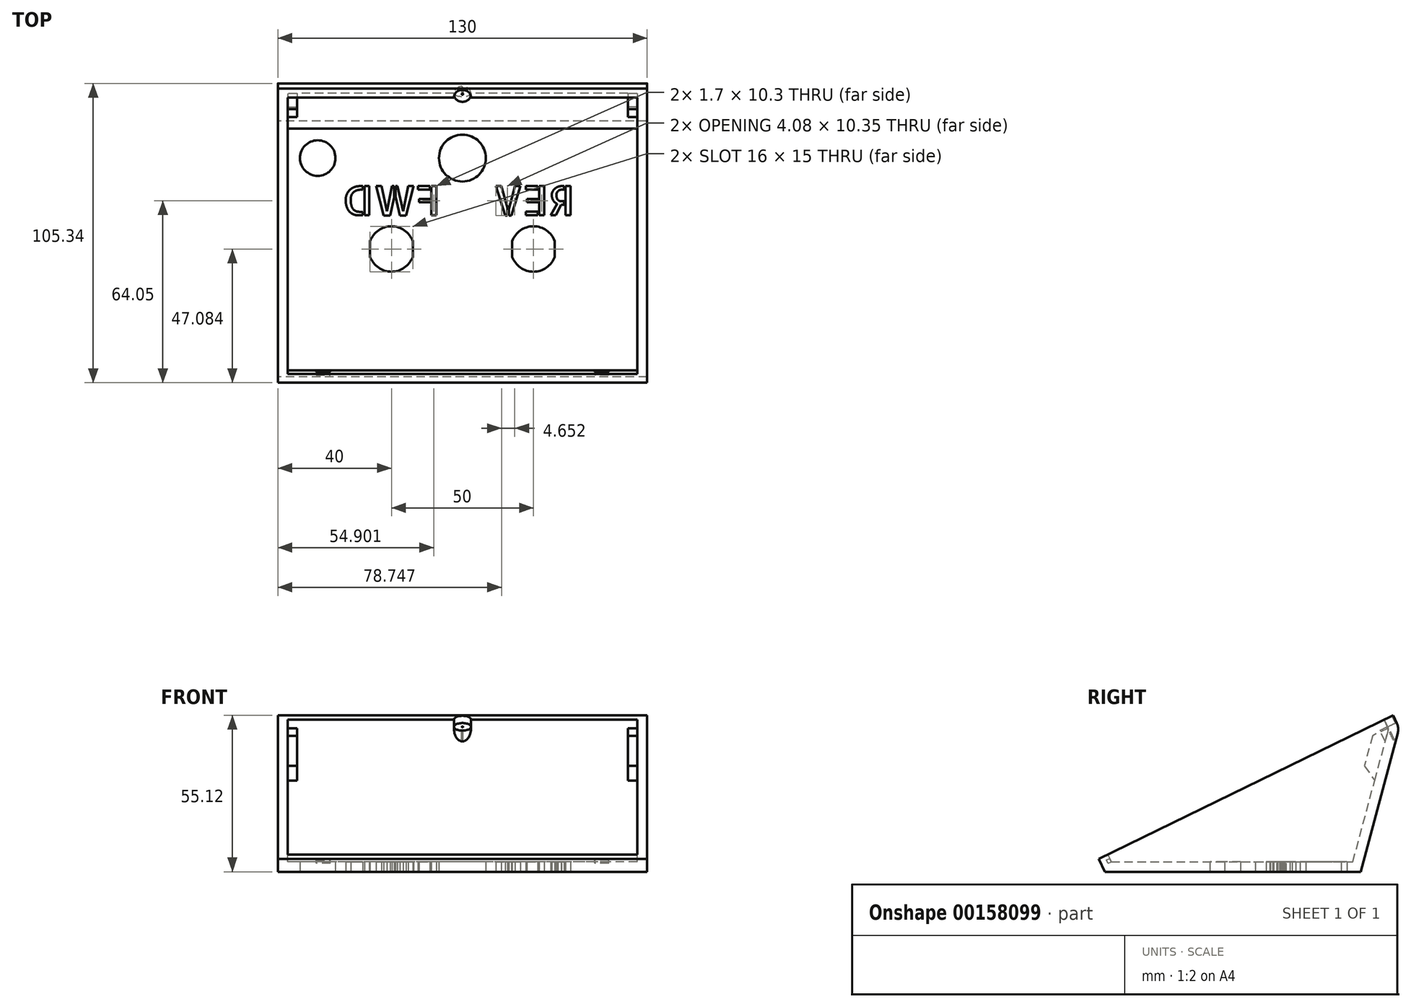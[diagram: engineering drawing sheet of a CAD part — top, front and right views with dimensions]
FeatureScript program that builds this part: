
annotation { "Feature Type Name" : "Feature", "Feature Type Description" : "" }
export const myFeature = defineFeature(function(context is Context, id is Id, definition is map)
    precondition{}
    {
        {
            var Q0;
            Q0=qCreatedBy(makeId("Right.planeOp"),FACE);
            var sketch = newSketch(context, id + "F0", { "sketchPlane" : qUnion([Q0])});
            skLineSegment(sketch, "E0", {"start": v(-41.87, 0) * mm, "end": v(48.13, 0) * mm});
            skLineSegment(sketch, "E1", {"start": v(48.13, 0) * mm, "end": v(61.22, 48.83) * mm});
            skLineSegment(sketch, "E2", {"start": v(60.93, 52.22) * mm, "end": v(59.6, 55.12) * mm});
            skLineSegment(sketch, "E3", {"start": v(59.6, 55.12) * mm, "end": v(-43.95, 4.54) * mm});
            skLineSegment(sketch, "E4", {"start": v(-43.95, 4.54) * mm, "end": v(-41.87, 0) * mm});
            skPoint(sketch, "E5.visualSharp", {"position": v(61.69, 50.58) * mm});
            skArc(sketch, "E5.filletArc", {"start": v(61.22, 48.83) * mm, "mid": v(61.37, 50.55) * mm, "end": v(60.93, 52.22) * mm});
            skSolve(sketch);
        }
        {
            var Q0;
            Q0=makeQuery(id+"F0.imprint","IMPRINT",FACE,{"disambiguationData":[TD([[makeQuery(id+"F0.imprint","IMPRINT",EDGE,{"derivedFrom":sQuery(id+"F0.wireOp",EDGE,"E0")}),1.0]])]});
            extrude(context, id + "F1", {"entities" : qUnion([Q0]), "depth" : 130 * mm});
        }
        {
            var Q0;
            Q0=makeQuery(id+"F1.opExtrude","SWEPT_FACE",FACE,{"disambiguationData":[OSD([sQuery(id+"F0.wireOp",EDGE,"E3")])]});
            shell(context, id + "F2", {"entities" : qUnion([Q0]), "thickness" : 3.5 * mm});
        }
        {
            var Q0;
            Q0=qCreatedBy(makeId("Top.planeOp"),FACE);
            var sketch = newSketch(context, id + "F3", { "sketchPlane" : qUnion([Q0])});
            skCircle(sketch, "E6", {"center": v(90, 3.13) * mm, "radius": 8 * mm});
            skPoint(sketch, "E7", {"position": v(82.5, 5.92) * mm});
            skPoint(sketch, "E8", {"position": v(82.5, 0.35) * mm});
            skPoint(sketch, "E9", {"position": v(97.5, 5.92) * mm});
            skPoint(sketch, "E10", {"position": v(97.5, 0.35) * mm});
            skLineSegment(sketch, "E11", {"start": v(82.5, 5.92) * mm, "end": v(82.5, 0.35) * mm});
            skLineSegment(sketch, "E12", {"start": v(97.5, 5.92) * mm, "end": v(97.5, 0.35) * mm});
            skCircle(sketch, "E13", {"center": v(40, 3.13) * mm, "radius": 8 * mm});
            skPoint(sketch, "E14", {"position": v(32.5, 5.92) * mm});
            skPoint(sketch, "E15", {"position": v(32.5, 0.35) * mm});
            skPoint(sketch, "E16", {"position": v(47.5, 5.92) * mm});
            skPoint(sketch, "E17", {"position": v(47.5, 0.35) * mm});
            skLineSegment(sketch, "E18", {"start": v(32.5, 5.92) * mm, "end": v(32.5, 0.35) * mm});
            skLineSegment(sketch, "E19", {"start": v(47.5, 5.92) * mm, "end": v(47.5, 0.35) * mm});
            skPoint(sketch, "E20", {"position": v(65, 3.3) * mm});
            skCircle(sketch, "E21", {"center": v(65, 35.13) * mm, "radius": 8.25 * mm});
            skCircle(sketch, "E22", {"center": v(14.06, 35.13) * mm, "radius": 6.25 * mm});
            skSolve(sketch);
        }
        {
            var Q0;
            {var subQ0=sQuery(id+"F3.wireOp",EDGE,"E11");Q0=makeQuery(id+"F3.imprint","IMPRINT",FACE,{"disambiguationData":[TD([[makeQuery(id+"F3.imprint","IMPRINT",EDGE,{"derivedFrom":subQ0}),1.0]])]});}
            var Q1;
            {var subQ0=sQuery(id+"F3.wireOp",EDGE,"E18");Q1=makeQuery(id+"F3.imprint","IMPRINT",FACE,{"disambiguationData":[TD([[makeQuery(id+"F3.imprint","IMPRINT",EDGE,{"derivedFrom":subQ0}),1.0]])]});}
            extrude(context, id + "F4", {"entities" : qUnion([Q0, Q1]), "operationType" : NewBodyOperationType.REMOVE, "depth" : 3.5 * mm});
        }
        {
            var Q0;
            Q0=qCreatedBy(makeId("Top.planeOp"),FACE);
            var sketch = newSketch(context, id + "F5", { "sketchPlane" : qUnion([Q0])});
            skText(sketch, "E23", { "text": "FWD", "fontName": "AllertaStencil-Regular.ttf"});
            skText(sketch, "E24", { "text": "REV", "fontName": "AllertaStencil-Regular.ttf"});
            skPoint(sketch, "E25", {"position": v(65, 28.3) * mm});
            const initialGuessF5  = {"E23": [0.07292, 0.01798, 1, 0, 0.0103], "E24": [0.02573, 0.01798, 1, 0, 0.0103]};
            skSetInitialGuess(sketch, initialGuessF5);
            skSolve(sketch);
        }
        {
            var Q0;
            Q0 = qSketchRegion(id + "F5", true);
            extrude(context, id + "F6", {"entities" : qUnion([Q0]), "depth" : 5 * mm});
        }
        {
            var Q0;
            Q0=makeQuery(id+"F6.opExtrude","SWEPT_BODY",BODY,{"disambiguationData":[OSD([sQuery(id+"F5.wireOp",EDGE,"E23.sketch_text.stroke-0"),sQuery(id+"F5.wireOp",EDGE,"E23.sketch_text.stroke-1"),sQuery(id+"F5.wireOp",EDGE,"E23.sketch_text.stroke-2"),sQuery(id+"F5.wireOp",EDGE,"E23.sketch_text.stroke-3")])]});
            var Q1;
            Q1=makeQuery(id+"F6.opExtrude","SWEPT_BODY",BODY,{"disambiguationData":[OSD([sQuery(id+"F5.wireOp",EDGE,"E23.sketch_text.stroke-4"),sQuery(id+"F5.wireOp",EDGE,"E23.sketch_text.stroke-5"),sQuery(id+"F5.wireOp",EDGE,"E23.sketch_text.stroke-6"),sQuery(id+"F5.wireOp",EDGE,"E23.sketch_text.stroke-7")])]});
            var Q2;
            Q2=makeQuery(id+"F6.opExtrude","SWEPT_BODY",BODY,{"disambiguationData":[OSD([sQuery(id+"F5.wireOp",EDGE,"E23.sketch_text.stroke-8"),sQuery(id+"F5.wireOp",EDGE,"E23.sketch_text.stroke-9"),sQuery(id+"F5.wireOp",EDGE,"E23.sketch_text.stroke-10"),sQuery(id+"F5.wireOp",EDGE,"E23.sketch_text.stroke-11")])]});
            var Q3;
            Q3=makeQuery(id+"F6.opExtrude","SWEPT_BODY",BODY,{"disambiguationData":[OSD([sQuery(id+"F5.wireOp",EDGE,"E23.sketch_text.stroke-12"),sQuery(id+"F5.wireOp",EDGE,"E23.sketch_text.stroke-13"),sQuery(id+"F5.wireOp",EDGE,"E23.sketch_text.stroke-14"),sQuery(id+"F5.wireOp",EDGE,"E23.sketch_text.stroke-15"),sQuery(id+"F5.wireOp",EDGE,"E23.sketch_text.stroke-16"),sQuery(id+"F5.wireOp",EDGE,"E23.sketch_text.stroke-17"),sQuery(id+"F5.wireOp",EDGE,"E23.sketch_text.stroke-18"),sQuery(id+"F5.wireOp",EDGE,"E23.sketch_text.stroke-19")])]});
            var Q4;
            Q4=makeQuery(id+"F6.opExtrude","SWEPT_BODY",BODY,{"disambiguationData":[OSD([sQuery(id+"F5.wireOp",EDGE,"E23.sketch_text.stroke-20"),sQuery(id+"F5.wireOp",EDGE,"E23.sketch_text.stroke-21"),sQuery(id+"F5.wireOp",EDGE,"E23.sketch_text.stroke-22"),sQuery(id+"F5.wireOp",EDGE,"E23.sketch_text.stroke-23"),sQuery(id+"F5.wireOp",EDGE,"E23.sketch_text.stroke-24"),sQuery(id+"F5.wireOp",EDGE,"E23.sketch_text.stroke-25"),sQuery(id+"F5.wireOp",EDGE,"E23.sketch_text.stroke-26"),sQuery(id+"F5.wireOp",EDGE,"E23.sketch_text.stroke-27")])]});
            var Q5;
            Q5=makeQuery(id+"F6.opExtrude","SWEPT_BODY",BODY,{"disambiguationData":[OSD([sQuery(id+"F5.wireOp",EDGE,"E23.sketch_text.stroke-28"),sQuery(id+"F5.wireOp",EDGE,"E23.sketch_text.stroke-29"),sQuery(id+"F5.wireOp",EDGE,"E23.sketch_text.stroke-30"),sQuery(id+"F5.wireOp",EDGE,"E23.sketch_text.stroke-31")])]});
            var Q6;
            Q6=makeQuery(id+"F6.opExtrude","SWEPT_BODY",BODY,{"disambiguationData":[OSD([sQuery(id+"F5.wireOp",EDGE,"E23.sketch_text.stroke-32"),sQuery(id+"F5.wireOp",EDGE,"E23.sketch_text.stroke-33"),sQuery(id+"F5.wireOp",EDGE,"E23.sketch_text.stroke-34"),sQuery(id+"F5.wireOp",EDGE,"E23.sketch_text.stroke-35"),sQuery(id+"F5.wireOp",EDGE,"E23.sketch_text.stroke-36"),sQuery(id+"F5.wireOp",EDGE,"E23.sketch_text.stroke-37"),sQuery(id+"F5.wireOp",EDGE,"E23.sketch_text.stroke-38"),sQuery(id+"F5.wireOp",EDGE,"E23.sketch_text.stroke-39"),sQuery(id+"F5.wireOp",EDGE,"E23.sketch_text.stroke-40"),sQuery(id+"F5.wireOp",EDGE,"E23.sketch_text.stroke-41"),sQuery(id+"F5.wireOp",EDGE,"E23.sketch_text.stroke-42"),sQuery(id+"F5.wireOp",EDGE,"E23.sketch_text.stroke-43"),sQuery(id+"F5.wireOp",EDGE,"E23.sketch_text.stroke-44"),sQuery(id+"F5.wireOp",EDGE,"E23.sketch_text.stroke-45"),sQuery(id+"F5.wireOp",EDGE,"E23.sketch_text.stroke-46"),sQuery(id+"F5.wireOp",EDGE,"E23.sketch_text.stroke-47"),sQuery(id+"F5.wireOp",EDGE,"E23.sketch_text.stroke-48"),sQuery(id+"F5.wireOp",EDGE,"E23.sketch_text.stroke-49"),sQuery(id+"F5.wireOp",EDGE,"E23.sketch_text.stroke-50"),sQuery(id+"F5.wireOp",EDGE,"E23.sketch_text.stroke-51"),sQuery(id+"F5.wireOp",EDGE,"E23.sketch_text.stroke-52"),sQuery(id+"F5.wireOp",EDGE,"E23.sketch_text.stroke-53")])]});
            var Q7;
            Q7=makeQuery(id+"F6.opExtrude","SWEPT_BODY",BODY,{"disambiguationData":[OSD([sQuery(id+"F5.wireOp",EDGE,"E24.sketch_text.stroke-0"),sQuery(id+"F5.wireOp",EDGE,"E24.sketch_text.stroke-1"),sQuery(id+"F5.wireOp",EDGE,"E24.sketch_text.stroke-2"),sQuery(id+"F5.wireOp",EDGE,"E24.sketch_text.stroke-3")])]});
            var Q8;
            Q8=makeQuery(id+"F6.opExtrude","SWEPT_BODY",BODY,{"disambiguationData":[OSD([sQuery(id+"F5.wireOp",EDGE,"E24.sketch_text.stroke-4"),sQuery(id+"F5.wireOp",EDGE,"E24.sketch_text.stroke-5"),sQuery(id+"F5.wireOp",EDGE,"E24.sketch_text.stroke-6"),sQuery(id+"F5.wireOp",EDGE,"E24.sketch_text.stroke-7"),sQuery(id+"F5.wireOp",EDGE,"E24.sketch_text.stroke-8"),sQuery(id+"F5.wireOp",EDGE,"E24.sketch_text.stroke-9"),sQuery(id+"F5.wireOp",EDGE,"E24.sketch_text.stroke-10"),sQuery(id+"F5.wireOp",EDGE,"E24.sketch_text.stroke-11"),sQuery(id+"F5.wireOp",EDGE,"E24.sketch_text.stroke-12"),sQuery(id+"F5.wireOp",EDGE,"E24.sketch_text.stroke-13"),sQuery(id+"F5.wireOp",EDGE,"E24.sketch_text.stroke-14"),sQuery(id+"F5.wireOp",EDGE,"E24.sketch_text.stroke-15"),sQuery(id+"F5.wireOp",EDGE,"E24.sketch_text.stroke-16"),sQuery(id+"F5.wireOp",EDGE,"E24.sketch_text.stroke-17"),sQuery(id+"F5.wireOp",EDGE,"E24.sketch_text.stroke-18"),sQuery(id+"F5.wireOp",EDGE,"E24.sketch_text.stroke-19"),sQuery(id+"F5.wireOp",EDGE,"E24.sketch_text.stroke-20"),sQuery(id+"F5.wireOp",EDGE,"E24.sketch_text.stroke-21"),sQuery(id+"F5.wireOp",EDGE,"E24.sketch_text.stroke-22"),sQuery(id+"F5.wireOp",EDGE,"E24.sketch_text.stroke-23"),sQuery(id+"F5.wireOp",EDGE,"E24.sketch_text.stroke-24"),sQuery(id+"F5.wireOp",EDGE,"E24.sketch_text.stroke-25"),sQuery(id+"F5.wireOp",EDGE,"E24.sketch_text.stroke-26"),sQuery(id+"F5.wireOp",EDGE,"E24.sketch_text.stroke-27"),sQuery(id+"F5.wireOp",EDGE,"E24.sketch_text.stroke-28"),sQuery(id+"F5.wireOp",EDGE,"E24.sketch_text.stroke-29")])]});
            var Q9;
            Q9=makeQuery(id+"F6.opExtrude","SWEPT_BODY",BODY,{"disambiguationData":[OSD([sQuery(id+"F5.wireOp",EDGE,"E24.sketch_text.stroke-30"),sQuery(id+"F5.wireOp",EDGE,"E24.sketch_text.stroke-31"),sQuery(id+"F5.wireOp",EDGE,"E24.sketch_text.stroke-32"),sQuery(id+"F5.wireOp",EDGE,"E24.sketch_text.stroke-33")])]});
            var Q10;
            Q10=makeQuery(id+"F6.opExtrude","SWEPT_BODY",BODY,{"disambiguationData":[OSD([sQuery(id+"F5.wireOp",EDGE,"E24.sketch_text.stroke-34"),sQuery(id+"F5.wireOp",EDGE,"E24.sketch_text.stroke-35"),sQuery(id+"F5.wireOp",EDGE,"E24.sketch_text.stroke-36"),sQuery(id+"F5.wireOp",EDGE,"E24.sketch_text.stroke-37")])]});
            var Q11;
            Q11=makeQuery(id+"F6.opExtrude","SWEPT_BODY",BODY,{"disambiguationData":[OSD([sQuery(id+"F5.wireOp",EDGE,"E24.sketch_text.stroke-38"),sQuery(id+"F5.wireOp",EDGE,"E24.sketch_text.stroke-39"),sQuery(id+"F5.wireOp",EDGE,"E24.sketch_text.stroke-40"),sQuery(id+"F5.wireOp",EDGE,"E24.sketch_text.stroke-41")])]});
            var Q12;
            Q12=makeQuery(id+"F6.opExtrude","SWEPT_BODY",BODY,{"disambiguationData":[OSD([sQuery(id+"F5.wireOp",EDGE,"E24.sketch_text.stroke-42"),sQuery(id+"F5.wireOp",EDGE,"E24.sketch_text.stroke-43"),sQuery(id+"F5.wireOp",EDGE,"E24.sketch_text.stroke-44"),sQuery(id+"F5.wireOp",EDGE,"E24.sketch_text.stroke-45")])]});
            var Q13;
            Q13=makeQuery(id+"F6.opExtrude","SWEPT_BODY",BODY,{"disambiguationData":[OSD([sQuery(id+"F5.wireOp",EDGE,"E24.sketch_text.stroke-46"),sQuery(id+"F5.wireOp",EDGE,"E24.sketch_text.stroke-47"),sQuery(id+"F5.wireOp",EDGE,"E24.sketch_text.stroke-48"),sQuery(id+"F5.wireOp",EDGE,"E24.sketch_text.stroke-49"),sQuery(id+"F5.wireOp",EDGE,"E24.sketch_text.stroke-50")])]});
            var Q14;
            Q14=makeQuery(id+"F6.opExtrude","SWEPT_BODY",BODY,{"disambiguationData":[OSD([sQuery(id+"F5.wireOp",EDGE,"E24.sketch_text.stroke-51"),sQuery(id+"F5.wireOp",EDGE,"E24.sketch_text.stroke-52"),sQuery(id+"F5.wireOp",EDGE,"E24.sketch_text.stroke-53"),sQuery(id+"F5.wireOp",EDGE,"E24.sketch_text.stroke-54"),sQuery(id+"F5.wireOp",EDGE,"E24.sketch_text.stroke-55")])]});
            var Q15;
            Q15=qCreatedBy(makeId("Right.planeOp"),FACE);
            mirror(context, id + "F7", {"entities" : qUnion([Q0, Q1, Q2, Q3, Q4, Q5, Q6, Q7, Q8, Q9, Q10, Q11, Q12, Q13, Q14]), "mirrorPlane" : qUnion([Q15])});
        }
        {
            var Q0;
            Q0=makeQuery(id+"F6.opExtrude","SWEPT_BODY",BODY,{"disambiguationData":[OSD([sQuery(id+"F5.wireOp",EDGE,"E23.sketch_text.stroke-0"),sQuery(id+"F5.wireOp",EDGE,"E23.sketch_text.stroke-1"),sQuery(id+"F5.wireOp",EDGE,"E23.sketch_text.stroke-2"),sQuery(id+"F5.wireOp",EDGE,"E23.sketch_text.stroke-3")])]});
            var Q1;
            Q1=makeQuery(id+"F6.opExtrude","SWEPT_BODY",BODY,{"disambiguationData":[OSD([sQuery(id+"F5.wireOp",EDGE,"E23.sketch_text.stroke-4"),sQuery(id+"F5.wireOp",EDGE,"E23.sketch_text.stroke-5"),sQuery(id+"F5.wireOp",EDGE,"E23.sketch_text.stroke-6"),sQuery(id+"F5.wireOp",EDGE,"E23.sketch_text.stroke-7")])]});
            var Q2;
            Q2=makeQuery(id+"F6.opExtrude","SWEPT_BODY",BODY,{"disambiguationData":[OSD([sQuery(id+"F5.wireOp",EDGE,"E23.sketch_text.stroke-8"),sQuery(id+"F5.wireOp",EDGE,"E23.sketch_text.stroke-9"),sQuery(id+"F5.wireOp",EDGE,"E23.sketch_text.stroke-10"),sQuery(id+"F5.wireOp",EDGE,"E23.sketch_text.stroke-11")])]});
            var Q3;
            Q3=makeQuery(id+"F6.opExtrude","SWEPT_BODY",BODY,{"disambiguationData":[OSD([sQuery(id+"F5.wireOp",EDGE,"E23.sketch_text.stroke-12"),sQuery(id+"F5.wireOp",EDGE,"E23.sketch_text.stroke-13"),sQuery(id+"F5.wireOp",EDGE,"E23.sketch_text.stroke-14"),sQuery(id+"F5.wireOp",EDGE,"E23.sketch_text.stroke-15"),sQuery(id+"F5.wireOp",EDGE,"E23.sketch_text.stroke-16"),sQuery(id+"F5.wireOp",EDGE,"E23.sketch_text.stroke-17"),sQuery(id+"F5.wireOp",EDGE,"E23.sketch_text.stroke-18"),sQuery(id+"F5.wireOp",EDGE,"E23.sketch_text.stroke-19")])]});
            var Q4;
            Q4=makeQuery(id+"F6.opExtrude","SWEPT_BODY",BODY,{"disambiguationData":[OSD([sQuery(id+"F5.wireOp",EDGE,"E23.sketch_text.stroke-20"),sQuery(id+"F5.wireOp",EDGE,"E23.sketch_text.stroke-21"),sQuery(id+"F5.wireOp",EDGE,"E23.sketch_text.stroke-22"),sQuery(id+"F5.wireOp",EDGE,"E23.sketch_text.stroke-23"),sQuery(id+"F5.wireOp",EDGE,"E23.sketch_text.stroke-24"),sQuery(id+"F5.wireOp",EDGE,"E23.sketch_text.stroke-25"),sQuery(id+"F5.wireOp",EDGE,"E23.sketch_text.stroke-26"),sQuery(id+"F5.wireOp",EDGE,"E23.sketch_text.stroke-27")])]});
            var Q5;
            Q5=makeQuery(id+"F6.opExtrude","SWEPT_BODY",BODY,{"disambiguationData":[OSD([sQuery(id+"F5.wireOp",EDGE,"E23.sketch_text.stroke-28"),sQuery(id+"F5.wireOp",EDGE,"E23.sketch_text.stroke-29"),sQuery(id+"F5.wireOp",EDGE,"E23.sketch_text.stroke-30"),sQuery(id+"F5.wireOp",EDGE,"E23.sketch_text.stroke-31")])]});
            var Q6;
            Q6=makeQuery(id+"F6.opExtrude","SWEPT_BODY",BODY,{"disambiguationData":[OSD([sQuery(id+"F5.wireOp",EDGE,"E23.sketch_text.stroke-32"),sQuery(id+"F5.wireOp",EDGE,"E23.sketch_text.stroke-33"),sQuery(id+"F5.wireOp",EDGE,"E23.sketch_text.stroke-34"),sQuery(id+"F5.wireOp",EDGE,"E23.sketch_text.stroke-35"),sQuery(id+"F5.wireOp",EDGE,"E23.sketch_text.stroke-36"),sQuery(id+"F5.wireOp",EDGE,"E23.sketch_text.stroke-37"),sQuery(id+"F5.wireOp",EDGE,"E23.sketch_text.stroke-38"),sQuery(id+"F5.wireOp",EDGE,"E23.sketch_text.stroke-39"),sQuery(id+"F5.wireOp",EDGE,"E23.sketch_text.stroke-40"),sQuery(id+"F5.wireOp",EDGE,"E23.sketch_text.stroke-41"),sQuery(id+"F5.wireOp",EDGE,"E23.sketch_text.stroke-42"),sQuery(id+"F5.wireOp",EDGE,"E23.sketch_text.stroke-43"),sQuery(id+"F5.wireOp",EDGE,"E23.sketch_text.stroke-44"),sQuery(id+"F5.wireOp",EDGE,"E23.sketch_text.stroke-45"),sQuery(id+"F5.wireOp",EDGE,"E23.sketch_text.stroke-46"),sQuery(id+"F5.wireOp",EDGE,"E23.sketch_text.stroke-47"),sQuery(id+"F5.wireOp",EDGE,"E23.sketch_text.stroke-48"),sQuery(id+"F5.wireOp",EDGE,"E23.sketch_text.stroke-49"),sQuery(id+"F5.wireOp",EDGE,"E23.sketch_text.stroke-50"),sQuery(id+"F5.wireOp",EDGE,"E23.sketch_text.stroke-51"),sQuery(id+"F5.wireOp",EDGE,"E23.sketch_text.stroke-52"),sQuery(id+"F5.wireOp",EDGE,"E23.sketch_text.stroke-53")])]});
            var Q7;
            Q7=makeQuery(id+"F6.opExtrude","SWEPT_BODY",BODY,{"disambiguationData":[OSD([sQuery(id+"F5.wireOp",EDGE,"E24.sketch_text.stroke-0"),sQuery(id+"F5.wireOp",EDGE,"E24.sketch_text.stroke-1"),sQuery(id+"F5.wireOp",EDGE,"E24.sketch_text.stroke-2"),sQuery(id+"F5.wireOp",EDGE,"E24.sketch_text.stroke-3")])]});
            var Q8;
            Q8=makeQuery(id+"F6.opExtrude","SWEPT_BODY",BODY,{"disambiguationData":[OSD([sQuery(id+"F5.wireOp",EDGE,"E24.sketch_text.stroke-4"),sQuery(id+"F5.wireOp",EDGE,"E24.sketch_text.stroke-5"),sQuery(id+"F5.wireOp",EDGE,"E24.sketch_text.stroke-6"),sQuery(id+"F5.wireOp",EDGE,"E24.sketch_text.stroke-7"),sQuery(id+"F5.wireOp",EDGE,"E24.sketch_text.stroke-8"),sQuery(id+"F5.wireOp",EDGE,"E24.sketch_text.stroke-9"),sQuery(id+"F5.wireOp",EDGE,"E24.sketch_text.stroke-10"),sQuery(id+"F5.wireOp",EDGE,"E24.sketch_text.stroke-11"),sQuery(id+"F5.wireOp",EDGE,"E24.sketch_text.stroke-12"),sQuery(id+"F5.wireOp",EDGE,"E24.sketch_text.stroke-13"),sQuery(id+"F5.wireOp",EDGE,"E24.sketch_text.stroke-14"),sQuery(id+"F5.wireOp",EDGE,"E24.sketch_text.stroke-15"),sQuery(id+"F5.wireOp",EDGE,"E24.sketch_text.stroke-16"),sQuery(id+"F5.wireOp",EDGE,"E24.sketch_text.stroke-17"),sQuery(id+"F5.wireOp",EDGE,"E24.sketch_text.stroke-18"),sQuery(id+"F5.wireOp",EDGE,"E24.sketch_text.stroke-19"),sQuery(id+"F5.wireOp",EDGE,"E24.sketch_text.stroke-20"),sQuery(id+"F5.wireOp",EDGE,"E24.sketch_text.stroke-21"),sQuery(id+"F5.wireOp",EDGE,"E24.sketch_text.stroke-22"),sQuery(id+"F5.wireOp",EDGE,"E24.sketch_text.stroke-23"),sQuery(id+"F5.wireOp",EDGE,"E24.sketch_text.stroke-24"),sQuery(id+"F5.wireOp",EDGE,"E24.sketch_text.stroke-25"),sQuery(id+"F5.wireOp",EDGE,"E24.sketch_text.stroke-26"),sQuery(id+"F5.wireOp",EDGE,"E24.sketch_text.stroke-27"),sQuery(id+"F5.wireOp",EDGE,"E24.sketch_text.stroke-28"),sQuery(id+"F5.wireOp",EDGE,"E24.sketch_text.stroke-29")])]});
            var Q9;
            Q9=makeQuery(id+"F6.opExtrude","SWEPT_BODY",BODY,{"disambiguationData":[OSD([sQuery(id+"F5.wireOp",EDGE,"E24.sketch_text.stroke-30"),sQuery(id+"F5.wireOp",EDGE,"E24.sketch_text.stroke-31"),sQuery(id+"F5.wireOp",EDGE,"E24.sketch_text.stroke-32"),sQuery(id+"F5.wireOp",EDGE,"E24.sketch_text.stroke-33")])]});
            var Q10;
            Q10=makeQuery(id+"F6.opExtrude","SWEPT_BODY",BODY,{"disambiguationData":[OSD([sQuery(id+"F5.wireOp",EDGE,"E24.sketch_text.stroke-34"),sQuery(id+"F5.wireOp",EDGE,"E24.sketch_text.stroke-35"),sQuery(id+"F5.wireOp",EDGE,"E24.sketch_text.stroke-36"),sQuery(id+"F5.wireOp",EDGE,"E24.sketch_text.stroke-37")])]});
            var Q11;
            Q11=makeQuery(id+"F6.opExtrude","SWEPT_BODY",BODY,{"disambiguationData":[OSD([sQuery(id+"F5.wireOp",EDGE,"E24.sketch_text.stroke-38"),sQuery(id+"F5.wireOp",EDGE,"E24.sketch_text.stroke-39"),sQuery(id+"F5.wireOp",EDGE,"E24.sketch_text.stroke-40"),sQuery(id+"F5.wireOp",EDGE,"E24.sketch_text.stroke-41")])]});
            var Q12;
            Q12=makeQuery(id+"F6.opExtrude","SWEPT_BODY",BODY,{"disambiguationData":[OSD([sQuery(id+"F5.wireOp",EDGE,"E24.sketch_text.stroke-42"),sQuery(id+"F5.wireOp",EDGE,"E24.sketch_text.stroke-43"),sQuery(id+"F5.wireOp",EDGE,"E24.sketch_text.stroke-44"),sQuery(id+"F5.wireOp",EDGE,"E24.sketch_text.stroke-45")])]});
            var Q13;
            Q13=makeQuery(id+"F6.opExtrude","SWEPT_BODY",BODY,{"disambiguationData":[OSD([sQuery(id+"F5.wireOp",EDGE,"E24.sketch_text.stroke-46"),sQuery(id+"F5.wireOp",EDGE,"E24.sketch_text.stroke-47"),sQuery(id+"F5.wireOp",EDGE,"E24.sketch_text.stroke-48"),sQuery(id+"F5.wireOp",EDGE,"E24.sketch_text.stroke-49"),sQuery(id+"F5.wireOp",EDGE,"E24.sketch_text.stroke-50")])]});
            var Q14;
            Q14=makeQuery(id+"F6.opExtrude","SWEPT_BODY",BODY,{"disambiguationData":[OSD([sQuery(id+"F5.wireOp",EDGE,"E24.sketch_text.stroke-51"),sQuery(id+"F5.wireOp",EDGE,"E24.sketch_text.stroke-52"),sQuery(id+"F5.wireOp",EDGE,"E24.sketch_text.stroke-53"),sQuery(id+"F5.wireOp",EDGE,"E24.sketch_text.stroke-54"),sQuery(id+"F5.wireOp",EDGE,"E24.sketch_text.stroke-55")])]});
            deleteBodies(context, id + "F8", {"entities" : qUnion([Q0, Q1, Q2, Q3, Q4, Q5, Q6, Q7, Q8, Q9, Q10, Q11, Q12, Q13, Q14])});
        }
        {
            var Q0;
            Q0=makeQuery(id+"F7.opPattern","COPY",BODY,{"derivedFrom":makeQuery(id+"F6.opExtrude","SWEPT_BODY",BODY,{"disambiguationData":[OSD([sQuery(id+"F5.wireOp",EDGE,"E23.sketch_text.stroke-0"),sQuery(id+"F5.wireOp",EDGE,"E23.sketch_text.stroke-1"),sQuery(id+"F5.wireOp",EDGE,"E23.sketch_text.stroke-2"),sQuery(id+"F5.wireOp",EDGE,"E23.sketch_text.stroke-3")])]}),"instanceName":"1"});
            var Q1;
            Q1=makeQuery(id+"F7.opPattern","COPY",BODY,{"derivedFrom":makeQuery(id+"F6.opExtrude","SWEPT_BODY",BODY,{"disambiguationData":[OSD([sQuery(id+"F5.wireOp",EDGE,"E23.sketch_text.stroke-4"),sQuery(id+"F5.wireOp",EDGE,"E23.sketch_text.stroke-5"),sQuery(id+"F5.wireOp",EDGE,"E23.sketch_text.stroke-6"),sQuery(id+"F5.wireOp",EDGE,"E23.sketch_text.stroke-7")])]}),"instanceName":"1"});
            var Q2;
            Q2=makeQuery(id+"F7.opPattern","COPY",BODY,{"derivedFrom":makeQuery(id+"F6.opExtrude","SWEPT_BODY",BODY,{"disambiguationData":[OSD([sQuery(id+"F5.wireOp",EDGE,"E23.sketch_text.stroke-8"),sQuery(id+"F5.wireOp",EDGE,"E23.sketch_text.stroke-9"),sQuery(id+"F5.wireOp",EDGE,"E23.sketch_text.stroke-10"),sQuery(id+"F5.wireOp",EDGE,"E23.sketch_text.stroke-11")])]}),"instanceName":"1"});
            var Q3;
            Q3=makeQuery(id+"F7.opPattern","COPY",BODY,{"derivedFrom":makeQuery(id+"F6.opExtrude","SWEPT_BODY",BODY,{"disambiguationData":[OSD([sQuery(id+"F5.wireOp",EDGE,"E23.sketch_text.stroke-12"),sQuery(id+"F5.wireOp",EDGE,"E23.sketch_text.stroke-13"),sQuery(id+"F5.wireOp",EDGE,"E23.sketch_text.stroke-14"),sQuery(id+"F5.wireOp",EDGE,"E23.sketch_text.stroke-15"),sQuery(id+"F5.wireOp",EDGE,"E23.sketch_text.stroke-16"),sQuery(id+"F5.wireOp",EDGE,"E23.sketch_text.stroke-17"),sQuery(id+"F5.wireOp",EDGE,"E23.sketch_text.stroke-18"),sQuery(id+"F5.wireOp",EDGE,"E23.sketch_text.stroke-19")])]}),"instanceName":"1"});
            var Q4;
            Q4=makeQuery(id+"F7.opPattern","COPY",BODY,{"derivedFrom":makeQuery(id+"F6.opExtrude","SWEPT_BODY",BODY,{"disambiguationData":[OSD([sQuery(id+"F5.wireOp",EDGE,"E23.sketch_text.stroke-20"),sQuery(id+"F5.wireOp",EDGE,"E23.sketch_text.stroke-21"),sQuery(id+"F5.wireOp",EDGE,"E23.sketch_text.stroke-22"),sQuery(id+"F5.wireOp",EDGE,"E23.sketch_text.stroke-23"),sQuery(id+"F5.wireOp",EDGE,"E23.sketch_text.stroke-24"),sQuery(id+"F5.wireOp",EDGE,"E23.sketch_text.stroke-25"),sQuery(id+"F5.wireOp",EDGE,"E23.sketch_text.stroke-26"),sQuery(id+"F5.wireOp",EDGE,"E23.sketch_text.stroke-27")])]}),"instanceName":"1"});
            var Q5;
            Q5=makeQuery(id+"F7.opPattern","COPY",BODY,{"derivedFrom":makeQuery(id+"F6.opExtrude","SWEPT_BODY",BODY,{"disambiguationData":[OSD([sQuery(id+"F5.wireOp",EDGE,"E23.sketch_text.stroke-28"),sQuery(id+"F5.wireOp",EDGE,"E23.sketch_text.stroke-29"),sQuery(id+"F5.wireOp",EDGE,"E23.sketch_text.stroke-30"),sQuery(id+"F5.wireOp",EDGE,"E23.sketch_text.stroke-31")])]}),"instanceName":"1"});
            var Q6;
            Q6=makeQuery(id+"F7.opPattern","COPY",BODY,{"derivedFrom":makeQuery(id+"F6.opExtrude","SWEPT_BODY",BODY,{"disambiguationData":[OSD([sQuery(id+"F5.wireOp",EDGE,"E23.sketch_text.stroke-32"),sQuery(id+"F5.wireOp",EDGE,"E23.sketch_text.stroke-33"),sQuery(id+"F5.wireOp",EDGE,"E23.sketch_text.stroke-34"),sQuery(id+"F5.wireOp",EDGE,"E23.sketch_text.stroke-35"),sQuery(id+"F5.wireOp",EDGE,"E23.sketch_text.stroke-36"),sQuery(id+"F5.wireOp",EDGE,"E23.sketch_text.stroke-37"),sQuery(id+"F5.wireOp",EDGE,"E23.sketch_text.stroke-38"),sQuery(id+"F5.wireOp",EDGE,"E23.sketch_text.stroke-39"),sQuery(id+"F5.wireOp",EDGE,"E23.sketch_text.stroke-40"),sQuery(id+"F5.wireOp",EDGE,"E23.sketch_text.stroke-41"),sQuery(id+"F5.wireOp",EDGE,"E23.sketch_text.stroke-42"),sQuery(id+"F5.wireOp",EDGE,"E23.sketch_text.stroke-43"),sQuery(id+"F5.wireOp",EDGE,"E23.sketch_text.stroke-44"),sQuery(id+"F5.wireOp",EDGE,"E23.sketch_text.stroke-45"),sQuery(id+"F5.wireOp",EDGE,"E23.sketch_text.stroke-46"),sQuery(id+"F5.wireOp",EDGE,"E23.sketch_text.stroke-47"),sQuery(id+"F5.wireOp",EDGE,"E23.sketch_text.stroke-48"),sQuery(id+"F5.wireOp",EDGE,"E23.sketch_text.stroke-49"),sQuery(id+"F5.wireOp",EDGE,"E23.sketch_text.stroke-50"),sQuery(id+"F5.wireOp",EDGE,"E23.sketch_text.stroke-51"),sQuery(id+"F5.wireOp",EDGE,"E23.sketch_text.stroke-52"),sQuery(id+"F5.wireOp",EDGE,"E23.sketch_text.stroke-53")])]}),"instanceName":"1"});
            var Q7;
            Q7=makeQuery(id+"F7.opPattern","COPY",BODY,{"derivedFrom":makeQuery(id+"F6.opExtrude","SWEPT_BODY",BODY,{"disambiguationData":[OSD([sQuery(id+"F5.wireOp",EDGE,"E24.sketch_text.stroke-0"),sQuery(id+"F5.wireOp",EDGE,"E24.sketch_text.stroke-1"),sQuery(id+"F5.wireOp",EDGE,"E24.sketch_text.stroke-2"),sQuery(id+"F5.wireOp",EDGE,"E24.sketch_text.stroke-3")])]}),"instanceName":"1"});
            var Q8;
            Q8=makeQuery(id+"F7.opPattern","COPY",BODY,{"derivedFrom":makeQuery(id+"F6.opExtrude","SWEPT_BODY",BODY,{"disambiguationData":[OSD([sQuery(id+"F5.wireOp",EDGE,"E24.sketch_text.stroke-4"),sQuery(id+"F5.wireOp",EDGE,"E24.sketch_text.stroke-5"),sQuery(id+"F5.wireOp",EDGE,"E24.sketch_text.stroke-6"),sQuery(id+"F5.wireOp",EDGE,"E24.sketch_text.stroke-7"),sQuery(id+"F5.wireOp",EDGE,"E24.sketch_text.stroke-8"),sQuery(id+"F5.wireOp",EDGE,"E24.sketch_text.stroke-9"),sQuery(id+"F5.wireOp",EDGE,"E24.sketch_text.stroke-10"),sQuery(id+"F5.wireOp",EDGE,"E24.sketch_text.stroke-11"),sQuery(id+"F5.wireOp",EDGE,"E24.sketch_text.stroke-12"),sQuery(id+"F5.wireOp",EDGE,"E24.sketch_text.stroke-13"),sQuery(id+"F5.wireOp",EDGE,"E24.sketch_text.stroke-14"),sQuery(id+"F5.wireOp",EDGE,"E24.sketch_text.stroke-15"),sQuery(id+"F5.wireOp",EDGE,"E24.sketch_text.stroke-16"),sQuery(id+"F5.wireOp",EDGE,"E24.sketch_text.stroke-17"),sQuery(id+"F5.wireOp",EDGE,"E24.sketch_text.stroke-18"),sQuery(id+"F5.wireOp",EDGE,"E24.sketch_text.stroke-19"),sQuery(id+"F5.wireOp",EDGE,"E24.sketch_text.stroke-20"),sQuery(id+"F5.wireOp",EDGE,"E24.sketch_text.stroke-21"),sQuery(id+"F5.wireOp",EDGE,"E24.sketch_text.stroke-22"),sQuery(id+"F5.wireOp",EDGE,"E24.sketch_text.stroke-23"),sQuery(id+"F5.wireOp",EDGE,"E24.sketch_text.stroke-24"),sQuery(id+"F5.wireOp",EDGE,"E24.sketch_text.stroke-25"),sQuery(id+"F5.wireOp",EDGE,"E24.sketch_text.stroke-26"),sQuery(id+"F5.wireOp",EDGE,"E24.sketch_text.stroke-27"),sQuery(id+"F5.wireOp",EDGE,"E24.sketch_text.stroke-28"),sQuery(id+"F5.wireOp",EDGE,"E24.sketch_text.stroke-29")])]}),"instanceName":"1"});
            var Q9;
            Q9=makeQuery(id+"F7.opPattern","COPY",BODY,{"derivedFrom":makeQuery(id+"F6.opExtrude","SWEPT_BODY",BODY,{"disambiguationData":[OSD([sQuery(id+"F5.wireOp",EDGE,"E24.sketch_text.stroke-30"),sQuery(id+"F5.wireOp",EDGE,"E24.sketch_text.stroke-31"),sQuery(id+"F5.wireOp",EDGE,"E24.sketch_text.stroke-32"),sQuery(id+"F5.wireOp",EDGE,"E24.sketch_text.stroke-33")])]}),"instanceName":"1"});
            var Q10;
            Q10=makeQuery(id+"F7.opPattern","COPY",BODY,{"derivedFrom":makeQuery(id+"F6.opExtrude","SWEPT_BODY",BODY,{"disambiguationData":[OSD([sQuery(id+"F5.wireOp",EDGE,"E24.sketch_text.stroke-34"),sQuery(id+"F5.wireOp",EDGE,"E24.sketch_text.stroke-35"),sQuery(id+"F5.wireOp",EDGE,"E24.sketch_text.stroke-36"),sQuery(id+"F5.wireOp",EDGE,"E24.sketch_text.stroke-37")])]}),"instanceName":"1"});
            var Q11;
            Q11=makeQuery(id+"F7.opPattern","COPY",BODY,{"derivedFrom":makeQuery(id+"F6.opExtrude","SWEPT_BODY",BODY,{"disambiguationData":[OSD([sQuery(id+"F5.wireOp",EDGE,"E24.sketch_text.stroke-38"),sQuery(id+"F5.wireOp",EDGE,"E24.sketch_text.stroke-39"),sQuery(id+"F5.wireOp",EDGE,"E24.sketch_text.stroke-40"),sQuery(id+"F5.wireOp",EDGE,"E24.sketch_text.stroke-41")])]}),"instanceName":"1"});
            var Q12;
            Q12=makeQuery(id+"F7.opPattern","COPY",BODY,{"derivedFrom":makeQuery(id+"F6.opExtrude","SWEPT_BODY",BODY,{"disambiguationData":[OSD([sQuery(id+"F5.wireOp",EDGE,"E24.sketch_text.stroke-42"),sQuery(id+"F5.wireOp",EDGE,"E24.sketch_text.stroke-43"),sQuery(id+"F5.wireOp",EDGE,"E24.sketch_text.stroke-44"),sQuery(id+"F5.wireOp",EDGE,"E24.sketch_text.stroke-45")])]}),"instanceName":"1"});
            var Q13;
            Q13=makeQuery(id+"F7.opPattern","COPY",BODY,{"derivedFrom":makeQuery(id+"F6.opExtrude","SWEPT_BODY",BODY,{"disambiguationData":[OSD([sQuery(id+"F5.wireOp",EDGE,"E24.sketch_text.stroke-46"),sQuery(id+"F5.wireOp",EDGE,"E24.sketch_text.stroke-47"),sQuery(id+"F5.wireOp",EDGE,"E24.sketch_text.stroke-48"),sQuery(id+"F5.wireOp",EDGE,"E24.sketch_text.stroke-49"),sQuery(id+"F5.wireOp",EDGE,"E24.sketch_text.stroke-50")])]}),"instanceName":"1"});
            var Q14;
            Q14=makeQuery(id+"F7.opPattern","COPY",BODY,{"derivedFrom":makeQuery(id+"F6.opExtrude","SWEPT_BODY",BODY,{"disambiguationData":[OSD([sQuery(id+"F5.wireOp",EDGE,"E24.sketch_text.stroke-51"),sQuery(id+"F5.wireOp",EDGE,"E24.sketch_text.stroke-52"),sQuery(id+"F5.wireOp",EDGE,"E24.sketch_text.stroke-53"),sQuery(id+"F5.wireOp",EDGE,"E24.sketch_text.stroke-54"),sQuery(id+"F5.wireOp",EDGE,"E24.sketch_text.stroke-55")])]}),"instanceName":"1"});
            transform(context, id + "F9", {"entities" : qUnion([Q0, Q1, Q2, Q3, Q4, Q5, Q6, Q7, Q8, Q9, Q10, Q11, Q12, Q13, Q14]), "transformType" : TransformType.TRANSLATION_3D, "dx" : 130 * mm, "dy" : -3 * mm, "dz" : 0 * mm, "makeCopy" : false});
        }
        {
            var Q0;
            Q0=makeQuery(id+"F7.opPattern","COPY",BODY,{"derivedFrom":makeQuery(id+"F6.opExtrude","SWEPT_BODY",BODY,{"disambiguationData":[OSD([sQuery(id+"F5.wireOp",EDGE,"E23.sketch_text.stroke-0"),sQuery(id+"F5.wireOp",EDGE,"E23.sketch_text.stroke-1"),sQuery(id+"F5.wireOp",EDGE,"E23.sketch_text.stroke-2"),sQuery(id+"F5.wireOp",EDGE,"E23.sketch_text.stroke-3")])]}),"instanceName":"1"});
            var Q1;
            Q1=makeQuery(id+"F7.opPattern","COPY",BODY,{"derivedFrom":makeQuery(id+"F6.opExtrude","SWEPT_BODY",BODY,{"disambiguationData":[OSD([sQuery(id+"F5.wireOp",EDGE,"E23.sketch_text.stroke-4"),sQuery(id+"F5.wireOp",EDGE,"E23.sketch_text.stroke-5"),sQuery(id+"F5.wireOp",EDGE,"E23.sketch_text.stroke-6"),sQuery(id+"F5.wireOp",EDGE,"E23.sketch_text.stroke-7")])]}),"instanceName":"1"});
            var Q2;
            Q2=makeQuery(id+"F7.opPattern","COPY",BODY,{"derivedFrom":makeQuery(id+"F6.opExtrude","SWEPT_BODY",BODY,{"disambiguationData":[OSD([sQuery(id+"F5.wireOp",EDGE,"E23.sketch_text.stroke-8"),sQuery(id+"F5.wireOp",EDGE,"E23.sketch_text.stroke-9"),sQuery(id+"F5.wireOp",EDGE,"E23.sketch_text.stroke-10"),sQuery(id+"F5.wireOp",EDGE,"E23.sketch_text.stroke-11")])]}),"instanceName":"1"});
            var Q3;
            Q3=makeQuery(id+"F7.opPattern","COPY",BODY,{"derivedFrom":makeQuery(id+"F6.opExtrude","SWEPT_BODY",BODY,{"disambiguationData":[OSD([sQuery(id+"F5.wireOp",EDGE,"E23.sketch_text.stroke-12"),sQuery(id+"F5.wireOp",EDGE,"E23.sketch_text.stroke-13"),sQuery(id+"F5.wireOp",EDGE,"E23.sketch_text.stroke-14"),sQuery(id+"F5.wireOp",EDGE,"E23.sketch_text.stroke-15"),sQuery(id+"F5.wireOp",EDGE,"E23.sketch_text.stroke-16"),sQuery(id+"F5.wireOp",EDGE,"E23.sketch_text.stroke-17"),sQuery(id+"F5.wireOp",EDGE,"E23.sketch_text.stroke-18"),sQuery(id+"F5.wireOp",EDGE,"E23.sketch_text.stroke-19")])]}),"instanceName":"1"});
            var Q4;
            Q4=makeQuery(id+"F7.opPattern","COPY",BODY,{"derivedFrom":makeQuery(id+"F6.opExtrude","SWEPT_BODY",BODY,{"disambiguationData":[OSD([sQuery(id+"F5.wireOp",EDGE,"E23.sketch_text.stroke-20"),sQuery(id+"F5.wireOp",EDGE,"E23.sketch_text.stroke-21"),sQuery(id+"F5.wireOp",EDGE,"E23.sketch_text.stroke-22"),sQuery(id+"F5.wireOp",EDGE,"E23.sketch_text.stroke-23"),sQuery(id+"F5.wireOp",EDGE,"E23.sketch_text.stroke-24"),sQuery(id+"F5.wireOp",EDGE,"E23.sketch_text.stroke-25"),sQuery(id+"F5.wireOp",EDGE,"E23.sketch_text.stroke-26"),sQuery(id+"F5.wireOp",EDGE,"E23.sketch_text.stroke-27")])]}),"instanceName":"1"});
            var Q5;
            Q5=makeQuery(id+"F7.opPattern","COPY",BODY,{"derivedFrom":makeQuery(id+"F6.opExtrude","SWEPT_BODY",BODY,{"disambiguationData":[OSD([sQuery(id+"F5.wireOp",EDGE,"E23.sketch_text.stroke-28"),sQuery(id+"F5.wireOp",EDGE,"E23.sketch_text.stroke-29"),sQuery(id+"F5.wireOp",EDGE,"E23.sketch_text.stroke-30"),sQuery(id+"F5.wireOp",EDGE,"E23.sketch_text.stroke-31")])]}),"instanceName":"1"});
            var Q6;
            Q6=makeQuery(id+"F7.opPattern","COPY",BODY,{"derivedFrom":makeQuery(id+"F6.opExtrude","SWEPT_BODY",BODY,{"disambiguationData":[OSD([sQuery(id+"F5.wireOp",EDGE,"E23.sketch_text.stroke-32"),sQuery(id+"F5.wireOp",EDGE,"E23.sketch_text.stroke-33"),sQuery(id+"F5.wireOp",EDGE,"E23.sketch_text.stroke-34"),sQuery(id+"F5.wireOp",EDGE,"E23.sketch_text.stroke-35"),sQuery(id+"F5.wireOp",EDGE,"E23.sketch_text.stroke-36"),sQuery(id+"F5.wireOp",EDGE,"E23.sketch_text.stroke-37"),sQuery(id+"F5.wireOp",EDGE,"E23.sketch_text.stroke-38"),sQuery(id+"F5.wireOp",EDGE,"E23.sketch_text.stroke-39"),sQuery(id+"F5.wireOp",EDGE,"E23.sketch_text.stroke-40"),sQuery(id+"F5.wireOp",EDGE,"E23.sketch_text.stroke-41"),sQuery(id+"F5.wireOp",EDGE,"E23.sketch_text.stroke-42"),sQuery(id+"F5.wireOp",EDGE,"E23.sketch_text.stroke-43"),sQuery(id+"F5.wireOp",EDGE,"E23.sketch_text.stroke-44"),sQuery(id+"F5.wireOp",EDGE,"E23.sketch_text.stroke-45"),sQuery(id+"F5.wireOp",EDGE,"E23.sketch_text.stroke-46"),sQuery(id+"F5.wireOp",EDGE,"E23.sketch_text.stroke-47"),sQuery(id+"F5.wireOp",EDGE,"E23.sketch_text.stroke-48"),sQuery(id+"F5.wireOp",EDGE,"E23.sketch_text.stroke-49"),sQuery(id+"F5.wireOp",EDGE,"E23.sketch_text.stroke-50"),sQuery(id+"F5.wireOp",EDGE,"E23.sketch_text.stroke-51"),sQuery(id+"F5.wireOp",EDGE,"E23.sketch_text.stroke-52"),sQuery(id+"F5.wireOp",EDGE,"E23.sketch_text.stroke-53")])]}),"instanceName":"1"});
            var Q7;
            Q7=makeQuery(id+"F7.opPattern","COPY",BODY,{"derivedFrom":makeQuery(id+"F6.opExtrude","SWEPT_BODY",BODY,{"disambiguationData":[OSD([sQuery(id+"F5.wireOp",EDGE,"E24.sketch_text.stroke-0"),sQuery(id+"F5.wireOp",EDGE,"E24.sketch_text.stroke-1"),sQuery(id+"F5.wireOp",EDGE,"E24.sketch_text.stroke-2"),sQuery(id+"F5.wireOp",EDGE,"E24.sketch_text.stroke-3")])]}),"instanceName":"1"});
            var Q8;
            Q8=makeQuery(id+"F7.opPattern","COPY",BODY,{"derivedFrom":makeQuery(id+"F6.opExtrude","SWEPT_BODY",BODY,{"disambiguationData":[OSD([sQuery(id+"F5.wireOp",EDGE,"E24.sketch_text.stroke-4"),sQuery(id+"F5.wireOp",EDGE,"E24.sketch_text.stroke-5"),sQuery(id+"F5.wireOp",EDGE,"E24.sketch_text.stroke-6"),sQuery(id+"F5.wireOp",EDGE,"E24.sketch_text.stroke-7"),sQuery(id+"F5.wireOp",EDGE,"E24.sketch_text.stroke-8"),sQuery(id+"F5.wireOp",EDGE,"E24.sketch_text.stroke-9"),sQuery(id+"F5.wireOp",EDGE,"E24.sketch_text.stroke-10"),sQuery(id+"F5.wireOp",EDGE,"E24.sketch_text.stroke-11"),sQuery(id+"F5.wireOp",EDGE,"E24.sketch_text.stroke-12"),sQuery(id+"F5.wireOp",EDGE,"E24.sketch_text.stroke-13"),sQuery(id+"F5.wireOp",EDGE,"E24.sketch_text.stroke-14"),sQuery(id+"F5.wireOp",EDGE,"E24.sketch_text.stroke-15"),sQuery(id+"F5.wireOp",EDGE,"E24.sketch_text.stroke-16"),sQuery(id+"F5.wireOp",EDGE,"E24.sketch_text.stroke-17"),sQuery(id+"F5.wireOp",EDGE,"E24.sketch_text.stroke-18"),sQuery(id+"F5.wireOp",EDGE,"E24.sketch_text.stroke-19"),sQuery(id+"F5.wireOp",EDGE,"E24.sketch_text.stroke-20"),sQuery(id+"F5.wireOp",EDGE,"E24.sketch_text.stroke-21"),sQuery(id+"F5.wireOp",EDGE,"E24.sketch_text.stroke-22"),sQuery(id+"F5.wireOp",EDGE,"E24.sketch_text.stroke-23"),sQuery(id+"F5.wireOp",EDGE,"E24.sketch_text.stroke-24"),sQuery(id+"F5.wireOp",EDGE,"E24.sketch_text.stroke-25"),sQuery(id+"F5.wireOp",EDGE,"E24.sketch_text.stroke-26"),sQuery(id+"F5.wireOp",EDGE,"E24.sketch_text.stroke-27"),sQuery(id+"F5.wireOp",EDGE,"E24.sketch_text.stroke-28"),sQuery(id+"F5.wireOp",EDGE,"E24.sketch_text.stroke-29")])]}),"instanceName":"1"});
            var Q9;
            Q9=makeQuery(id+"F7.opPattern","COPY",BODY,{"derivedFrom":makeQuery(id+"F6.opExtrude","SWEPT_BODY",BODY,{"disambiguationData":[OSD([sQuery(id+"F5.wireOp",EDGE,"E24.sketch_text.stroke-30"),sQuery(id+"F5.wireOp",EDGE,"E24.sketch_text.stroke-31"),sQuery(id+"F5.wireOp",EDGE,"E24.sketch_text.stroke-32"),sQuery(id+"F5.wireOp",EDGE,"E24.sketch_text.stroke-33")])]}),"instanceName":"1"});
            var Q10;
            Q10=makeQuery(id+"F7.opPattern","COPY",BODY,{"derivedFrom":makeQuery(id+"F6.opExtrude","SWEPT_BODY",BODY,{"disambiguationData":[OSD([sQuery(id+"F5.wireOp",EDGE,"E24.sketch_text.stroke-34"),sQuery(id+"F5.wireOp",EDGE,"E24.sketch_text.stroke-35"),sQuery(id+"F5.wireOp",EDGE,"E24.sketch_text.stroke-36"),sQuery(id+"F5.wireOp",EDGE,"E24.sketch_text.stroke-37")])]}),"instanceName":"1"});
            var Q11;
            Q11=makeQuery(id+"F7.opPattern","COPY",BODY,{"derivedFrom":makeQuery(id+"F6.opExtrude","SWEPT_BODY",BODY,{"disambiguationData":[OSD([sQuery(id+"F5.wireOp",EDGE,"E24.sketch_text.stroke-38"),sQuery(id+"F5.wireOp",EDGE,"E24.sketch_text.stroke-39"),sQuery(id+"F5.wireOp",EDGE,"E24.sketch_text.stroke-40"),sQuery(id+"F5.wireOp",EDGE,"E24.sketch_text.stroke-41")])]}),"instanceName":"1"});
            var Q12;
            Q12=makeQuery(id+"F7.opPattern","COPY",BODY,{"derivedFrom":makeQuery(id+"F6.opExtrude","SWEPT_BODY",BODY,{"disambiguationData":[OSD([sQuery(id+"F5.wireOp",EDGE,"E24.sketch_text.stroke-42"),sQuery(id+"F5.wireOp",EDGE,"E24.sketch_text.stroke-43"),sQuery(id+"F5.wireOp",EDGE,"E24.sketch_text.stroke-44"),sQuery(id+"F5.wireOp",EDGE,"E24.sketch_text.stroke-45")])]}),"instanceName":"1"});
            var Q13;
            Q13=makeQuery(id+"F7.opPattern","COPY",BODY,{"derivedFrom":makeQuery(id+"F6.opExtrude","SWEPT_BODY",BODY,{"disambiguationData":[OSD([sQuery(id+"F5.wireOp",EDGE,"E24.sketch_text.stroke-46"),sQuery(id+"F5.wireOp",EDGE,"E24.sketch_text.stroke-47"),sQuery(id+"F5.wireOp",EDGE,"E24.sketch_text.stroke-48"),sQuery(id+"F5.wireOp",EDGE,"E24.sketch_text.stroke-49"),sQuery(id+"F5.wireOp",EDGE,"E24.sketch_text.stroke-50")])]}),"instanceName":"1"});
            var Q14;
            Q14=makeQuery(id+"F7.opPattern","COPY",BODY,{"derivedFrom":makeQuery(id+"F6.opExtrude","SWEPT_BODY",BODY,{"disambiguationData":[OSD([sQuery(id+"F5.wireOp",EDGE,"E24.sketch_text.stroke-51"),sQuery(id+"F5.wireOp",EDGE,"E24.sketch_text.stroke-52"),sQuery(id+"F5.wireOp",EDGE,"E24.sketch_text.stroke-53"),sQuery(id+"F5.wireOp",EDGE,"E24.sketch_text.stroke-54"),sQuery(id+"F5.wireOp",EDGE,"E24.sketch_text.stroke-55")])]}),"instanceName":"1"});
            var Q15;
            Q15=makeQuery(id+"F1.opExtrude","SWEPT_BODY",BODY,{"disambiguationData":[OSD([sQuery(id+"F0.wireOp",EDGE,"E0"),sQuery(id+"F0.wireOp",EDGE,"E1"),sQuery(id+"F0.wireOp",EDGE,"E2"),sQuery(id+"F0.wireOp",EDGE,"E3"),sQuery(id+"F0.wireOp",EDGE,"E4"),sQuery(id+"F0.wireOp",EDGE,"E5.filletArc")])]});
            booleanBodies(context, id + "F10", {"operationType" : BooleanOperationType.SUBTRACTION, "tools" : qUnion([Q0, Q1, Q2, Q3, Q4, Q5, Q6, Q7, Q8, Q9, Q10, Q11, Q12, Q13, Q14]), "targets" : qUnion([Q15])});
        }
        {
            var Q0;
            Q0=makeQuery(id+"F3.imprint","IMPRINT",FACE,{"disambiguationData":[TD([[makeQuery(id+"F3.imprint","IMPRINT",EDGE,{"derivedFrom":sQuery(id+"F3.wireOp",EDGE,"E21")}),1.0]])]});
            extrude(context, id + "F11", {"entities" : qUnion([Q0]), "operationType" : NewBodyOperationType.REMOVE, "depth" : 3.5 * mm});
        }
        {
            var Q0;
            Q0=makeQuery(id+"F2.opShell","OFFSET_FACE",FACE,{"disambiguationData":[OSD([sQuery(id+"F0.wireOp",EDGE,"E4")])]});
            var sketch = newSketch(context, id + "F12", { "sketchPlane" : qUnion([Q0])});
            skLineSegment(sketch, "E26.bottom", {"start": v(-13.5, 19.73) * mm, "end": v(-18.5, 19.73) * mm});
            skLineSegment(sketch, "E26.top", {"start": v(-13.5, 20.98) * mm, "end": v(-18.5, 20.98) * mm});
            skLineSegment(sketch, "E26.left", {"start": v(-13.5, 19.73) * mm, "end": v(-13.5, 20.98) * mm});
            skLineSegment(sketch, "E26.right", {"start": v(-18.5, 19.73) * mm, "end": v(-18.5, 20.98) * mm});
            skLineSegment(sketch, "E27.bottom", {"start": v(-116.5, 19.73) * mm, "end": v(-111.5, 19.73) * mm});
            skLineSegment(sketch, "E27.top", {"start": v(-116.5, 20.98) * mm, "end": v(-111.5, 20.98) * mm});
            skLineSegment(sketch, "E27.left", {"start": v(-116.5, 19.73) * mm, "end": v(-116.5, 20.98) * mm});
            skLineSegment(sketch, "E27.right", {"start": v(-111.5, 19.73) * mm, "end": v(-111.5, 20.98) * mm});
            skPoint(sketch, "E28", {"position": v(-105.27, 19.73) * mm});
            skPoint(sketch, "E29", {"position": v(-105.27, 22.57) * mm});
            skSolve(sketch);
        }
        {
            var Q0;
            Q0 = qSketchRegion(id + "F12", true);
            extrude(context, id + "F13", {"entities" : qUnion([Q0]), "operationType" : NewBodyOperationType.REMOVE, "oppositeDirection" : true, "depth" : 1.25 * mm});
        }
        {
            var Q0;
            Q0=makeQuery(id+"F1.opExtrude","SWEPT_FACE",FACE,{"disambiguationData":[OSD([sQuery(id+"F0.wireOp",EDGE,"E3")])]});
            var sketch = newSketch(context, id + "F14", { "sketchPlane" : qUnion([Q0])});
            skCircle(sketch, "E30", {"center": v(65, 74.24) * mm, "radius": 3 * mm});
            skSolve(sketch);
        }
        {
            var Q0;
            Q0 = qSketchRegion(id + "F14", true);
            extrude(context, id + "F15", {"entities" : qUnion([Q0]), "operationType" : NewBodyOperationType.REMOVE, "oppositeDirection" : true, "depth" : 2.84 * mm});
        }
        {
            var Q0;
            Q0=makeQuery(id+"F15.boolean.opBoolean","COPY",FACE,{"derivedFrom":makeQuery(id+"F15.opExtrude","CAP_FACE",FACE,{"disambiguationData":[OSD([sQuery(id+"F14.wireOp",EDGE,"E30")])],"isStart":false})});
            var sketch = newSketch(context, id + "F16", { "sketchPlane" : qUnion([Q0])});
            skArc(sketch, "E31", {"start": v(62, 74.17) * mm, "mid": v(65, 71.18) * mm, "end": v(68, 74.17) * mm});
            skLineSegment(sketch, "E32", {"start": v(62, 74.17) * mm, "end": v(68, 74.17) * mm});
            skSolve(sketch);
        }
        {
            var Q0;
            Q0 = qSketchRegion(id + "F16", true);
            extrude(context, id + "F17", {"entities" : qUnion([Q0]), "operationType" : NewBodyOperationType.ADD, "oppositeDirection" : true, "depth" : 5.75 * mm});
        }
        {
            var Q0;
            Q0=sQuery(id+"F16.wireOp",VERTEX,"E31.center");
            var Q1;
            Q1=makeQuery(id+"F1.opExtrude","SWEPT_BODY",BODY,{"disambiguationData":[OSD([sQuery(id+"F0.wireOp",EDGE,"E0"),sQuery(id+"F0.wireOp",EDGE,"E1"),sQuery(id+"F0.wireOp",EDGE,"E2"),sQuery(id+"F0.wireOp",EDGE,"E3"),sQuery(id+"F0.wireOp",EDGE,"E4"),sQuery(id+"F0.wireOp",EDGE,"E5.filletArc")])]});
            hole(context, id + "F18", {"style" : HoleStyle.SIMPLE, "endStyle" : HoleEndStyle.BLIND, "holeDiameter" : .5 * mm, "holeDepth" : 5 * mm, "startFromSketch" : true, "locations" : qUnion([Q0]), "scope" : qUnion([Q1])});
        }
        {
            var Q0;
            Q0=makeQuery(id+"F3.imprint","IMPRINT",FACE,{"disambiguationData":[TD([[makeQuery(id+"F3.imprint","IMPRINT",EDGE,{"derivedFrom":sQuery(id+"F3.wireOp",EDGE,"E22")}),1.0]])]});
            extrude(context, id + "F19", {"entities" : qUnion([Q0]), "operationType" : NewBodyOperationType.REMOVE, "depth" : 3.5 * mm});
        }
        {
            var Q0;
            {var subQ0=sQuery(id+"F0.wireOp",EDGE,"E5.filletArc");var subQ1=sQuery(id+"F0.wireOp",EDGE,"E4");var subQ2=sQuery(id+"F0.wireOp",EDGE,"E3");var subQ3=sQuery(id+"F0.wireOp",EDGE,"E2");var subQ4=sQuery(id+"F0.wireOp",EDGE,"E1");var subQ5=sQuery(id+"F0.wireOp",EDGE,"E0");Q0=makeQuery(id+"F2.opShell","OFFSET_FACE",FACE,{"disambiguationData":[OSD([subQ5,subQ4,subQ3,subQ2,subQ1,subQ0]),TDD([makeQuery(id+"F1.opExtrude","CAP_FACE",FACE,{"disambiguationData":[OSD([subQ5,subQ4,subQ3,subQ2,subQ1,subQ0])],"isStart":false})])]});}
            var sketch = newSketch(context, id + "F20", { "sketchPlane" : qUnion([Q0])});
            skLineSegment(sketch, "E33", {"start": v(-45.45, 3.5) * mm, "end": v(-58.1, 50.69) * mm});
            skLineSegment(sketch, "E34", {"start": v(-58.1, 50.69) * mm, "end": v(-52.34, 47.88) * mm});
            skLineSegment(sketch, "E35", {"start": v(-52.34, 47.88) * mm, "end": v(-40.45, 3.5) * mm});
            skLineSegment(sketch, "E36", {"start": v(-40.45, 3.5) * mm, "end": v(-45.45, 3.5) * mm});
            skSolve(sketch);
        }
        {
            var Q0;
            Q0 = qSketchRegion(id + "F20", true);
            extrude(context, id + "F21", {"entities" : qUnion([Q0]), "operationType" : NewBodyOperationType.ADD, "depth" : 3.25 * mm});
        }
        {
            var Q0;
            {var subQ0=sQuery(id+"F0.wireOp",EDGE,"E5.filletArc");var subQ1=sQuery(id+"F0.wireOp",EDGE,"E4");var subQ2=sQuery(id+"F0.wireOp",EDGE,"E3");var subQ3=sQuery(id+"F0.wireOp",EDGE,"E2");var subQ4=sQuery(id+"F0.wireOp",EDGE,"E1");var subQ5=sQuery(id+"F0.wireOp",EDGE,"E0");Q0=makeQuery(id+"F2.opShell","OFFSET_FACE",FACE,{"disambiguationData":[OSD([subQ5,subQ4,subQ3,subQ2,subQ1,subQ0]),TDD([makeQuery(id+"F1.opExtrude","CAP_FACE",FACE,{"disambiguationData":[OSD([subQ5,subQ4,subQ3,subQ2,subQ1,subQ0])],"isStart":true})])]});}
            var sketch = newSketch(context, id + "F22", { "sketchPlane" : qUnion([Q0])});
            skLineSegment(sketch, "E37", {"start": v(45.45, 3.5) * mm, "end": v(58.1, 50.69) * mm});
            skLineSegment(sketch, "E38", {"start": v(58.1, 50.69) * mm, "end": v(52.34, 47.88) * mm});
            skLineSegment(sketch, "E39", {"start": v(52.34, 47.88) * mm, "end": v(40.45, 3.5) * mm});
            skLineSegment(sketch, "E40", {"start": v(40.45, 3.5) * mm, "end": v(45.45, 3.5) * mm});
            skSolve(sketch);
        }
        {
            var Q0;
            Q0 = qSketchRegion(id + "F22", true);
            extrude(context, id + "F23", {"entities" : qUnion([Q0]), "operationType" : NewBodyOperationType.ADD, "depth" : 3.25 * mm});
        }
        {
            var Q0;
            Q0=makeQuery(id+"F23.opExtrude","CAP_FACE",FACE,{"disambiguationData":[OSD([sQuery(id+"F22.wireOp",EDGE,"E37"),sQuery(id+"F22.wireOp",EDGE,"E38"),sQuery(id+"F22.wireOp",EDGE,"E39"),sQuery(id+"F22.wireOp",EDGE,"E40")])],"isStart":false});
            var sketch = newSketch(context, id + "F24", { "sketchPlane" : qUnion([Q0])});
            skLineSegment(sketch, "E41", {"start": v(49.5, 37.3) * mm, "end": v(53.12, 32.14) * mm});
            skLineSegment(sketch, "E42", {"start": v(53.12, 32.14) * mm, "end": v(45.45, 3.5) * mm});
            skLineSegment(sketch, "E43", {"start": v(45.45, 3.5) * mm, "end": v(40.45, 3.5) * mm});
            skLineSegment(sketch, "E44", {"start": v(40.45, 3.5) * mm, "end": v(49.5, 37.3) * mm});
            skSolve(sketch);
        }
        {
            var Q0;
            Q0 = qSketchRegion(id + "F24", true);
            extrude(context, id + "F25", {"entities" : qUnion([Q0]), "operationType" : NewBodyOperationType.REMOVE, "oppositeDirection" : true, "depth" : 3.25 * mm});
        }
        {
            var Q0;
            Q0=makeQuery(id+"F21.opExtrude","CAP_FACE",FACE,{"disambiguationData":[OSD([sQuery(id+"F20.wireOp",EDGE,"E33"),sQuery(id+"F20.wireOp",EDGE,"E34"),sQuery(id+"F20.wireOp",EDGE,"E35"),sQuery(id+"F20.wireOp",EDGE,"E36")])],"isStart":false});
            var sketch = newSketch(context, id + "F26", { "sketchPlane" : qUnion([Q0])});
            skLineSegment(sketch, "E45", {"start": v(-40.45, 3.5) * mm, "end": v(-49.5, 37.3) * mm});
            skLineSegment(sketch, "E46", {"start": v(-49.5, 37.3) * mm, "end": v(-53.12, 32.14) * mm});
            skLineSegment(sketch, "E47", {"start": v(-53.12, 32.14) * mm, "end": v(-45.45, 3.5) * mm});
            skLineSegment(sketch, "E48", {"start": v(-45.45, 3.5) * mm, "end": v(-40.45, 3.5) * mm});
            skSolve(sketch);
        }
        {
            var Q0;
            Q0 = qSketchRegion(id + "F26", true);
            extrude(context, id + "F27", {"entities" : qUnion([Q0]), "operationType" : NewBodyOperationType.REMOVE, "oppositeDirection" : true, "depth" : 3.25 * mm});
        }
    });
